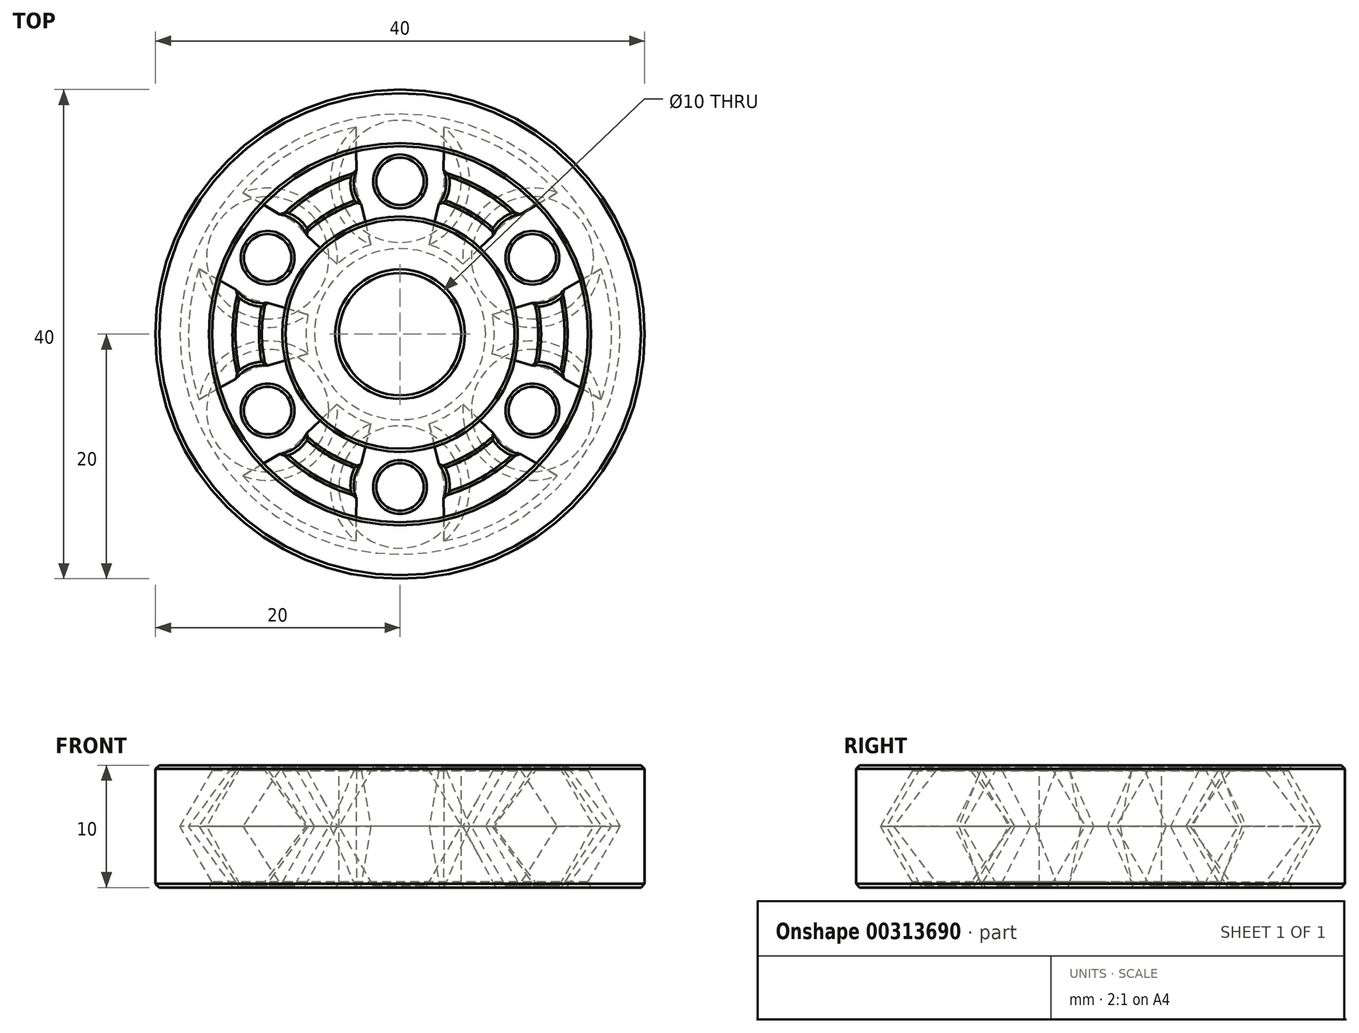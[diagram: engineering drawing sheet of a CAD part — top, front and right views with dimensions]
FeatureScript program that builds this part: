
annotation { "Feature Type Name" : "Feature", "Feature Type Description" : "" }
export const myFeature = defineFeature(function(context is Context, id is Id, definition is map)
    precondition{}
    {
        {
            var Q0;
            Q0=qCreatedBy(makeId("Top.planeOp"),FACE);
            var sketch = newSketch(context, id + "F0", { "sketchPlane" : qUnion([Q0])});
            skCircle(sketch, "E0", {"center": v(0, 0) * mm, "radius": 5 * mm});
            skCircle(sketch, "E1", {"center": v(0, 0) * mm, "radius": 20 * mm});
            skSolve(sketch);
        }
        {
            var Q0;
            Q0=qCreatedBy(makeId("Right.planeOp"),FACE);
            var sketch = newSketch(context, id + "F1", { "sketchPlane" : qUnion([Q0])});
            skLineSegment(sketch, "E2", {"start": v(0, 25) * mm, "end": v(0, -25) * mm, "construction": true});
            skSolve(sketch);
        }
        {
            var Q0;
            Q0=qCreatedBy(makeId("Right.planeOp"),FACE);
            var sketch = newSketch(context, id + "F2", { "sketchPlane" : qUnion([Q0])});
            skLineSegment(sketch, "E3", {"start": v(-5, 5) * mm, "end": v(-5, -5) * mm});
            skLineSegment(sketch, "E4", {"start": v(-5, 5) * mm, "end": v(-9.89, 5) * mm});
            skLineSegment(sketch, "E5", {"start": v(-9.89, 5) * mm, "end": v(-7, 0) * mm});
            skLineSegment(sketch, "E6", {"start": v(-7, 0) * mm, "end": v(-9.89, -5) * mm});
            skLineSegment(sketch, "E7", {"start": v(-9.89, -5) * mm, "end": v(-5, -5) * mm});
            skLineSegment(sketch, "E8", {"start": v(-7, 0) * mm, "end": v(-5, 0) * mm, "construction": true});
            skLineSegment(sketch, "E9", {"start": v(-15.11, 5) * mm, "end": v(-20, 5) * mm});
            skLineSegment(sketch, "E10", {"start": v(-20, 5) * mm, "end": v(-20, -5) * mm});
            skLineSegment(sketch, "E11", {"start": v(-20, -5) * mm, "end": v(-15.11, -5) * mm});
            skLineSegment(sketch, "E12", {"start": v(-15.11, -5) * mm, "end": v(-18, 0) * mm});
            skLineSegment(sketch, "E13", {"start": v(-18, 0) * mm, "end": v(-15.11, 5) * mm});
            skLineSegment(sketch, "E14", {"start": v(-14.61, 5) * mm, "end": v(-10.39, 5) * mm});
            skLineSegment(sketch, "E15", {"start": v(-10.39, 5) * mm, "end": v(-7.5, 0) * mm});
            skLineSegment(sketch, "E16", {"start": v(-7.5, 0) * mm, "end": v(-10.39, -5) * mm});
            skLineSegment(sketch, "E17", {"start": v(-10.39, -5) * mm, "end": v(-14.61, -5) * mm});
            skLineSegment(sketch, "E18", {"start": v(-14.61, -5) * mm, "end": v(-17.5, 0) * mm});
            skLineSegment(sketch, "E19", {"start": v(-17.5, 0) * mm, "end": v(-14.61, 5) * mm});
            skLineSegment(sketch, "E20", {"start": v(-15.11, 5) * mm, "end": v(-14.61, 5) * mm, "construction": true});
            skLineSegment(sketch, "E21", {"start": v(-10.39, 5) * mm, "end": v(-9.89, 5) * mm, "construction": true});
            skLineSegment(sketch, "E22", {"start": v(-10.39, -5) * mm, "end": v(-9.89, -5) * mm, "construction": true});
            skLineSegment(sketch, "E23", {"start": v(-15.11, -5) * mm, "end": v(-14.61, -5) * mm, "construction": true});
            skPoint(sketch, "E24", {"position": v(-12.5, 5) * mm});
            skPoint(sketch, "E25", {"position": v(-12.5, -5) * mm});
            skPoint(sketch, "E26", {"position": v(-12.5, 0) * mm});
            skLineSegment(sketch, "E27", {"start": v(-12.5, 10) * mm, "end": v(-12.5, -10) * mm, "construction": true});
            skSolve(sketch);
        }
        {
            var Q0;
            Q0=qCreatedBy(makeId("Right.planeOp"),FACE);
            var sketch = newSketch(context, id + "F3", { "sketchPlane" : qUnion([Q0])});
            skLineSegment(sketch, "E28.0", {"start": v(-9.89, 5) * mm, "end": v(-7, 0) * mm});
            skLineSegment(sketch, "E28.1", {"start": v(-5, 5) * mm, "end": v(-9.89, 5) * mm});
            skLineSegment(sketch, "E28.2", {"start": v(-5, 5) * mm, "end": v(-5, -5) * mm});
            skLineSegment(sketch, "E28.3", {"start": v(-7, 0) * mm, "end": v(-9.89, -5) * mm});
            skLineSegment(sketch, "E28.4", {"start": v(-9.89, -5) * mm, "end": v(-5, -5) * mm});
            skLineSegment(sketch, "E28.5", {"start": v(-15.11, -5) * mm, "end": v(-18, 0) * mm});
            skLineSegment(sketch, "E28.6", {"start": v(-18, 0) * mm, "end": v(-15.11, 5) * mm});
            skLineSegment(sketch, "E28.7", {"start": v(-15.11, 5) * mm, "end": v(-20, 5) * mm});
            skLineSegment(sketch, "E28.8", {"start": v(-20, 5) * mm, "end": v(-20, -5) * mm});
            skLineSegment(sketch, "E28.9", {"start": v(-20, -5) * mm, "end": v(-15.11, -5) * mm});
            skSolve(sketch);
        }
        {
            var Q0;
            Q0=qSketchRegion(id+"F3",true);
            var Q1;
            Q1=sQuery(id+"F1.wireOp",EDGE,"E2");
            revolve(context, id + "F4", {"entities" : qUnion([Q0]), "axis" : qUnion([Q1]), "revolveType" : RevolveType.FULL});
        }
        {
            var Q0;
            Q0=qCreatedBy(makeId("Right.planeOp"),FACE);
            var sketch = newSketch(context, id + "F5", { "sketchPlane" : qUnion([Q0])});
            skLineSegment(sketch, "E29.0", {"start": v(-17.5, 0) * mm, "end": v(-14.61, 5) * mm});
            skLineSegment(sketch, "E29.1", {"start": v(-14.61, 5) * mm, "end": v(-12.5, 5) * mm});
            skLineSegment(sketch, "E29.2", {"start": v(-14.61, -5) * mm, "end": v(-17.5, 0) * mm});
            skLineSegment(sketch, "E29.3", {"start": v(-12.5, -5) * mm, "end": v(-14.61, -5) * mm});
            skLineSegment(sketch, "E30", {"start": v(-12.5, 5) * mm, "end": v(-12.5, -5) * mm});
            skPoint(sketch, "E31.orphan", {"position": v(-10.39, 5) * mm});
            skPoint(sketch, "E32.orphan", {"position": v(-10.39, -5) * mm});
            skSolve(sketch);
        }
        {
            var Q0;
            Q0=qSketchRegion(id+"F5",true);
            var Q1;
            Q1=sQuery(id+"F2.wireOp",EDGE,"E27");
            revolve(context, id + "F6", {"entities" : qUnion([Q0]), "axis" : qUnion([Q1]), "revolveType" : RevolveType.FULL});
        }
        {
            var Q0;
            Q0=makeQuery(id+"F6.opRevolve","SWEPT_BODY",BODY,{"disambiguationData":[OSD([sQuery(id+"F5.wireOp",EDGE,"E29.0"),sQuery(id+"F5.wireOp",EDGE,"E29.1"),sQuery(id+"F5.wireOp",EDGE,"E29.2"),sQuery(id+"F5.wireOp",EDGE,"E29.3"),sQuery(id+"F5.wireOp",EDGE,"E30")])]});
            var Q1;
            Q1=sQuery(id+"F1.wireOp",EDGE,"E2");
            circularPattern(context, id + "F7", {"entities" : qUnion([Q0]), "axis" : qUnion([Q1]), "angle" : 60 * degree, "instanceCount" : 6});
        }
        {
            var Q0;
            Q0=qCreatedBy(makeId("Top.planeOp"),FACE);
            var sketch = newSketch(context, id + "F8", { "sketchPlane" : qUnion([Q0])});
            skCircle(sketch, "E33.0", {"center": v(10.83, 6.25) * mm, "radius": 5 * mm, "construction": true});
            skArc(sketch, "E34", {"start": v(7.53, -1.6) * mm, "mid": v(7.7, 0) * mm, "end": v(7.53, 1.6) * mm});
            skArc(sketch, "E35.trimOffspring", {"start": v(7.53, 1.6) * mm, "mid": v(13.03, 1) * mm, "end": v(16.45, 5.35) * mm});
            skArc(sketch, "E36.trimOffspring", {"start": v(16.45, -5.35) * mm, "mid": v(13.03, -1) * mm, "end": v(7.53, -1.6) * mm});
            skArc(sketch, "E37.trimOffspring", {"start": v(16.45, -5.35) * mm, "mid": v(17.3, 0) * mm, "end": v(16.45, 5.35) * mm});
            skSolve(sketch);
        }
        {
            var Q0;
            Q0=makeQuery(id+"F4.opRevolve","SWEPT_FACE",FACE,{"disambiguationData":[OSD([sQuery(id+"F3.wireOp",EDGE,"E28.1")])]});
            var sketch = newSketch(context, id + "F9", { "sketchPlane" : qUnion([Q0])});
            skArc(sketch, "E38.0", {"start": v(11.08, -2.65) * mm, "mid": v(11.39, 0) * mm, "end": v(11.08, 2.65) * mm});
            skArc(sketch, "E39.0", {"start": v(11.08, 2.65) * mm, "mid": v(12.18, 2.9) * mm, "end": v(13.16, 3.5) * mm});
            skArc(sketch, "E40.0", {"start": v(13.16, -3.5) * mm, "mid": v(12.18, -2.9) * mm, "end": v(11.08, -2.65) * mm});
            skArc(sketch, "E41.0", {"start": v(13.16, -3.5) * mm, "mid": v(13.61, 0) * mm, "end": v(13.16, 3.5) * mm});
            skSolve(sketch);
        }
        {
            var Q0;
            Q0=makeQuery(id+"F4.opRevolve","SWEPT_FACE",FACE,{"disambiguationData":[OSD([sQuery(id+"F3.wireOp",EDGE,"E28.9")])]});
            var sketch = newSketch(context, id + "F10", { "sketchPlane" : qUnion([Q0])});
            skArc(sketch, "E42.0", {"start": v(13.16, 3.5) * mm, "mid": v(13.61, 0) * mm, "end": v(13.16, -3.5) * mm});
            skArc(sketch, "E42.1", {"start": v(11.08, -2.65) * mm, "mid": v(12.18, -2.9) * mm, "end": v(13.16, -3.5) * mm});
            skArc(sketch, "E42.2", {"start": v(11.08, 2.65) * mm, "mid": v(11.39, 0) * mm, "end": v(11.08, -2.65) * mm});
            skArc(sketch, "E42.3", {"start": v(13.16, 3.5) * mm, "mid": v(12.18, 2.9) * mm, "end": v(11.08, 2.65) * mm});
            skSolve(sketch);
        }
        {
            var Q0;
            Q0=qSketchRegion(id+"F9",true);
            var Q1;
            Q1=qSketchRegion(id+"F8",true);
            loft(context, id + "F11", {"sheetProfilesArray" : [{ "sheetProfileEntities" : qUnion([Q0]) }, { "sheetProfileEntities" : qUnion([Q1]) }]});
        }
        {
            var Q1;
            Q1=qSketchRegion(id+"F8",true);
            var Q2;
            Q2=qSketchRegion(id+"F10",true);
            loft(context, id + "F12", {"operationType" : NewBodyOperationType.ADD, "sheetProfilesArray" : [{ "sheetProfileEntities" : qUnion([Q1]) }, { "sheetProfileEntities" : qUnion([Q2]) }]});
        }
        {
            var Q0;
            Q0=makeQuery(id+"F11.opLoft","SWEPT_BODY",BODY,{"disambiguationData":[OSD([makeQuery(id+"F8.imprint","IMPRINT",FACE,{"disambiguationData":[TD([[makeQuery(id+"F8.imprint","IMPRINT",EDGE,{"derivedFrom":sQuery(id+"F8.wireOp",EDGE,"E34")}),-1.0]])]}),makeQuery(id+"F9.imprint","IMPRINT",FACE,{"disambiguationData":[TD([[makeQuery(id+"F9.imprint","IMPRINT",EDGE,{"derivedFrom":sQuery(id+"F9.wireOp",EDGE,"E38.0")}),-1.0]])]})])]});
            var Q1;
            Q1=sQuery(id+"F1.wireOp",EDGE,"E2");
            circularPattern(context, id + "F13", {"entities" : qUnion([Q0]), "axis" : qUnion([Q1]), "angle" : 60 * degree, "instanceCount" : 6});
        }
        {
            var Q0;
            Q0=makeQuery(id+"F4.opRevolve","SWEPT_FACE",FACE,{"disambiguationData":[OSD([sQuery(id+"F3.wireOp",EDGE,"E28.7")])]});
            var Q1;
            Q1=makeQuery(id+"F4.opRevolve","SWEPT_FACE",FACE,{"disambiguationData":[OSD([sQuery(id+"F3.wireOp",EDGE,"E28.1")])]});
            var Q2;
            Q2=makeQuery(id+"F13.opPattern","COPY",FACE,{"derivedFrom":makeQuery(id+"F11.opLoft","CAP_FACE",FACE,{"disambiguationData":[OSD([makeQuery(id+"F9.imprint","IMPRINT",FACE,{"disambiguationData":[TD([[makeQuery(id+"F9.imprint","IMPRINT",EDGE,{"derivedFrom":sQuery(id+"F9.wireOp",EDGE,"E38.0")}),-1.0]])]})])],"isStart":true}),"instanceName":"1"});
            var Q3;
            Q3=makeQuery(id+"F7.opPattern","COPY",FACE,{"derivedFrom":makeQuery(id+"F6.opRevolve","SWEPT_FACE",FACE,{"disambiguationData":[OSD([sQuery(id+"F5.wireOp",EDGE,"E29.1")])]}),"instanceName":"5"});
            var Q4;
            Q4=makeQuery(id+"F11.opLoft","CAP_FACE",FACE,{"disambiguationData":[OSD([makeQuery(id+"F9.imprint","IMPRINT",FACE,{"disambiguationData":[TD([[makeQuery(id+"F9.imprint","IMPRINT",EDGE,{"derivedFrom":sQuery(id+"F9.wireOp",EDGE,"E38.0")}),-1.0]])]})])],"isStart":true});
            var Q5;
            Q5=makeQuery(id+"F7.opPattern","COPY",FACE,{"derivedFrom":makeQuery(id+"F6.opRevolve","SWEPT_FACE",FACE,{"disambiguationData":[OSD([sQuery(id+"F5.wireOp",EDGE,"E29.1")])]}),"instanceName":"4"});
            var Q6;
            Q6=makeQuery(id+"F13.opPattern","COPY",FACE,{"derivedFrom":makeQuery(id+"F11.opLoft","CAP_FACE",FACE,{"disambiguationData":[OSD([makeQuery(id+"F9.imprint","IMPRINT",FACE,{"disambiguationData":[TD([[makeQuery(id+"F9.imprint","IMPRINT",EDGE,{"derivedFrom":sQuery(id+"F9.wireOp",EDGE,"E38.0")}),-1.0]])]})])],"isStart":true}),"instanceName":"5"});
            var Q7;
            Q7=makeQuery(id+"F7.opPattern","COPY",FACE,{"derivedFrom":makeQuery(id+"F6.opRevolve","SWEPT_FACE",FACE,{"disambiguationData":[OSD([sQuery(id+"F5.wireOp",EDGE,"E29.1")])]}),"instanceName":"3"});
            var Q8;
            Q8=makeQuery(id+"F13.opPattern","COPY",FACE,{"derivedFrom":makeQuery(id+"F11.opLoft","CAP_FACE",FACE,{"disambiguationData":[OSD([makeQuery(id+"F9.imprint","IMPRINT",FACE,{"disambiguationData":[TD([[makeQuery(id+"F9.imprint","IMPRINT",EDGE,{"derivedFrom":sQuery(id+"F9.wireOp",EDGE,"E38.0")}),-1.0]])]})])],"isStart":true}),"instanceName":"4"});
            var Q9;
            Q9=makeQuery(id+"F7.opPattern","COPY",FACE,{"derivedFrom":makeQuery(id+"F6.opRevolve","SWEPT_FACE",FACE,{"disambiguationData":[OSD([sQuery(id+"F5.wireOp",EDGE,"E29.1")])]}),"instanceName":"2"});
            var Q10;
            Q10=makeQuery(id+"F13.opPattern","COPY",FACE,{"derivedFrom":makeQuery(id+"F11.opLoft","CAP_FACE",FACE,{"disambiguationData":[OSD([makeQuery(id+"F9.imprint","IMPRINT",FACE,{"disambiguationData":[TD([[makeQuery(id+"F9.imprint","IMPRINT",EDGE,{"derivedFrom":sQuery(id+"F9.wireOp",EDGE,"E38.0")}),-1.0]])]})])],"isStart":true}),"instanceName":"3"});
            var Q11;
            Q11=makeQuery(id+"F7.opPattern","COPY",FACE,{"derivedFrom":makeQuery(id+"F6.opRevolve","SWEPT_FACE",FACE,{"disambiguationData":[OSD([sQuery(id+"F5.wireOp",EDGE,"E29.1")])]}),"instanceName":"1"});
            var Q12;
            Q12=makeQuery(id+"F13.opPattern","COPY",FACE,{"derivedFrom":makeQuery(id+"F11.opLoft","CAP_FACE",FACE,{"disambiguationData":[OSD([makeQuery(id+"F9.imprint","IMPRINT",FACE,{"disambiguationData":[TD([[makeQuery(id+"F9.imprint","IMPRINT",EDGE,{"derivedFrom":sQuery(id+"F9.wireOp",EDGE,"E38.0")}),-1.0]])]})])],"isStart":true}),"instanceName":"2"});
            var Q13;
            Q13=makeQuery(id+"F6.opRevolve","SWEPT_FACE",FACE,{"disambiguationData":[OSD([sQuery(id+"F5.wireOp",EDGE,"E29.1")])]});
            var Q14;
            Q14=makeQuery(id+"F4.opRevolve","SWEPT_EDGE",EDGE,{"disambiguationData":[OSD([sQuery(id+"F3.wireOp",EDGE,"E28.8"),sQuery(id+"F3.wireOp",EDGE,"E28.9")])]});
            var Q15;
            Q15=makeQuery(id+"F7.opPattern","COPY",EDGE,{"derivedFrom":makeQuery(id+"F6.opRevolve","SWEPT_EDGE",EDGE,{"disambiguationData":[OSD([sQuery(id+"F5.wireOp",EDGE,"E29.2"),sQuery(id+"F5.wireOp",EDGE,"E29.3")])]}),"instanceName":"5"});
            var Q16;
            Q16=makeQuery(id+"F4.opRevolve","SWEPT_EDGE",EDGE,{"disambiguationData":[OSD([sQuery(id+"F3.wireOp",EDGE,"E28.5"),sQuery(id+"F3.wireOp",EDGE,"E28.9")])]});
            var Q17;
            Q17=makeQuery(id+"F4.opRevolve","SWEPT_FACE",FACE,{"disambiguationData":[OSD([sQuery(id+"F3.wireOp",EDGE,"E28.4")])]});
            var Q18;
            Q18=makeQuery(id+"F12.opLoft","CAP_FACE",FACE,{"disambiguationData":[OSD([makeQuery(id+"F10.imprint","IMPRINT",FACE,{"disambiguationData":[TD([[makeQuery(id+"F10.imprint","IMPRINT",EDGE,{"derivedFrom":sQuery(id+"F10.wireOp",EDGE,"E42.0")}),-1.0]])]})])],"isStart":true});
            var Q19;
            Q19=makeQuery(id+"F7.opPattern","COPY",FACE,{"derivedFrom":makeQuery(id+"F6.opRevolve","SWEPT_FACE",FACE,{"disambiguationData":[OSD([sQuery(id+"F5.wireOp",EDGE,"E29.3")])]}),"instanceName":"4"});
            var Q20;
            Q20=makeQuery(id+"F13.opPattern","COPY",FACE,{"derivedFrom":makeQuery(id+"F12.opLoft","CAP_FACE",FACE,{"disambiguationData":[OSD([makeQuery(id+"F10.imprint","IMPRINT",FACE,{"disambiguationData":[TD([[makeQuery(id+"F10.imprint","IMPRINT",EDGE,{"derivedFrom":sQuery(id+"F10.wireOp",EDGE,"E42.0")}),-1.0]])]})])],"isStart":true}),"instanceName":"5"});
            var Q21;
            Q21=makeQuery(id+"F7.opPattern","COPY",FACE,{"derivedFrom":makeQuery(id+"F6.opRevolve","SWEPT_FACE",FACE,{"disambiguationData":[OSD([sQuery(id+"F5.wireOp",EDGE,"E29.3")])]}),"instanceName":"3"});
            var Q22;
            Q22=makeQuery(id+"F13.opPattern","COPY",FACE,{"derivedFrom":makeQuery(id+"F12.opLoft","CAP_FACE",FACE,{"disambiguationData":[OSD([makeQuery(id+"F10.imprint","IMPRINT",FACE,{"disambiguationData":[TD([[makeQuery(id+"F10.imprint","IMPRINT",EDGE,{"derivedFrom":sQuery(id+"F10.wireOp",EDGE,"E42.0")}),-1.0]])]})])],"isStart":true}),"instanceName":"4"});
            var Q23;
            Q23=makeQuery(id+"F7.opPattern","COPY",FACE,{"derivedFrom":makeQuery(id+"F6.opRevolve","SWEPT_FACE",FACE,{"disambiguationData":[OSD([sQuery(id+"F5.wireOp",EDGE,"E29.3")])]}),"instanceName":"2"});
            var Q24;
            Q24=makeQuery(id+"F13.opPattern","COPY",FACE,{"derivedFrom":makeQuery(id+"F12.opLoft","CAP_FACE",FACE,{"disambiguationData":[OSD([makeQuery(id+"F10.imprint","IMPRINT",FACE,{"disambiguationData":[TD([[makeQuery(id+"F10.imprint","IMPRINT",EDGE,{"derivedFrom":sQuery(id+"F10.wireOp",EDGE,"E42.0")}),-1.0]])]})])],"isStart":true}),"instanceName":"3"});
            var Q25;
            Q25=makeQuery(id+"F7.opPattern","COPY",FACE,{"derivedFrom":makeQuery(id+"F6.opRevolve","SWEPT_FACE",FACE,{"disambiguationData":[OSD([sQuery(id+"F5.wireOp",EDGE,"E29.3")])]}),"instanceName":"1"});
            var Q26;
            Q26=makeQuery(id+"F13.opPattern","COPY",FACE,{"derivedFrom":makeQuery(id+"F12.opLoft","CAP_FACE",FACE,{"disambiguationData":[OSD([makeQuery(id+"F10.imprint","IMPRINT",FACE,{"disambiguationData":[TD([[makeQuery(id+"F10.imprint","IMPRINT",EDGE,{"derivedFrom":sQuery(id+"F10.wireOp",EDGE,"E42.0")}),-1.0]])]})])],"isStart":true}),"instanceName":"2"});
            var Q27;
            Q27=makeQuery(id+"F6.opRevolve","SWEPT_FACE",FACE,{"disambiguationData":[OSD([sQuery(id+"F5.wireOp",EDGE,"E29.3")])]});
            chamfer(context, id + "F14", {"entities" : qUnion([Q0, Q1, Q2, Q3, Q4, Q5, Q6, Q7, Q8, Q9, Q10, Q11, Q12, Q13, Q14, Q15, Q16, Q17, Q18, Q19, Q20, Q21, Q22, Q23, Q24, Q25, Q26, Q27]), "width" : 0.3 * mm, "tangentPropagation" : true});
        }
    });
